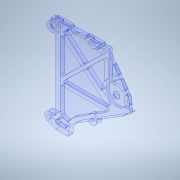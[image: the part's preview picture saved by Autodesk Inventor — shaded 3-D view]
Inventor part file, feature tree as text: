
AUTODESK INVENTOR PART (.ipt)
format: ipt  version: 2020.2 (Build 242310000, 310)  size: 1,882,112 bytes
history: native  units: mm
features: sketch x33, extrude x32, projected_geometry x28, fillet x11, other x4, hole x3
ambient origin geometry x8: Origin, YZ Plane, XZ Plane, XY Plane, X Axis, Y Axis, Z Axis, Center Point
bodies: Body1 (feature_tree)
feature tree (111):
  other  "ソリッド1"
  sketch  "スケッチ1"
  extrude  "押し出し1"  Depth=5.0mm
  extrude  "押し出し2"  Depth=3.0mm
  extrude  "押し出し3"  Depth=5.0mm
  extrude  "押し出し4"  Depth=3.0mm
  sketch  "スケッチ4"
  extrude  "押し出し5"  Depth=3.0mm
  extrude  "押し出し6"  Depth=5.0mm
  extrude  "押し出し7"  Depth=1.0mm
  sketch  "スケッチ6"
  extrude  "押し出し8"  Depth=5.0mm
  extrude  "押し出し9"  Depth=5.0mm
  sketch  "スケッチ8"
  extrude  "押し出し10"  Depth=2.0mm
  extrude  "押し出し11"  Depth=2.0mm
  extrude  "押し出し12"  Depth=2.0mm
  extrude  "押し出し13"  Depth=2.0mm
  sketch  "スケッチ9"
  extrude  "押し出し14"  Depth=2.0mm
  extrude  "押し出し15"  Depth=2.0mm
  sketch  "スケッチ10"
  sketch  "スケッチ11"
  sketch  "スケッチ12"
  sketch  "スケッチ13"
  extrude  "押し出し16"  Depth=2.0mm
  hole  "穴1"  [1 undecoded]
  fillet  "フィレット1"  Radius=2.0mm
  fillet  "フィレット2"  Radius=2.0mm
  sketch  "スケッチ14"
  sketch  "スケッチ15"
  extrude  "押し出し17"  Depth=2.0mm
  extrude  "押し出し18"  Depth=2.0mm
  sketch  "スケッチ16"
  extrude  "押し出し19"  Depth=5.0mm TaperAngle=0.0deg
  extrude  "押し出し20"  Depth=2.55mm TaperAngle=0.0deg
  hole  "穴2"  [1 undecoded]
  extrude  "押し出し21"  Depth=3.0mm TaperAngle=0.0deg
  fillet  "フィレット3"  Radius=2.0mm
  sketch  "スケッチ18"
  sketch  "スケッチ19"
  extrude  "押し出し22"  Depth=3.0mm TaperAngle=0.0deg
  fillet  "フィレット4"  Radius=3.0mm
  sketch  "スケッチ20"
  extrude  "押し出し23"  Depth=2.55mm TaperAngle=0.0deg
  fillet  "フィレット5"  Radius=5.0mm
  extrude  "押し出し24"  Depth=2.0mm TaperAngle=0.0deg
  fillet  "フィレット6"  Radius=9.0mm
  extrude  "押し出し25"  Depth=3.0mm
  fillet  "フィレット7"  Radius=10.0mm
  extrude  "押し出し26"  Depth=2.0mm
  fillet  "フィレット8"  Radius=2.0mm
  sketch  "スケッチ25"
  sketch  "スケッチ26"
  extrude  "押し出し27"  Depth=2.0mm
  sketch  "スケッチ27"
  sketch  "スケッチ28"
  extrude  "押し出し28"  Depth=2.0mm
  hole  "穴3"  [1 undecoded]
  fillet  "フィレット9"  Radius=3.0mm
  extrude  "押し出し29"  Depth=3.0mm
  extrude  "押し出し30"  Depth=3.0mm
  fillet  "フィレット10"  Radius=15.0mm
  extrude  "押し出し31"  Depth=15.0mm
  fillet  "フィレット11"  Radius=3.0mm
  sketch  "スケッチ32"
  extrude  "押し出し32"  Depth=3.0mm
  sketch  "スケッチ2"
  projected_geometry  "投影ループ1"
  sketch  "スケッチ3"
  projected_geometry  "投影ループ2"
  projected_geometry  "投影ループ3"
  sketch  "スケッチ5"
  projected_geometry  "投影ループ4"
  projected_geometry  "投影ループ5"
  projected_geometry  "投影ループ6"
  sketch  "スケッチ7"
  projected_geometry  "投影ループ7"
  projected_geometry  "投影ループ8"
  projected_geometry  "投影ループ9"
  projected_geometry  "投影ループ10"
  projected_geometry  "投影ループ11"
  projected_geometry  "投影ループ12"
  projected_geometry  "投影ループ13"
  projected_geometry  "投影ループ14"
  projected_geometry  "投影ループ15"
  sketch  "スケッチ17"
  projected_geometry  "投影ループ16"
  projected_geometry  "投影ループ17"
  projected_geometry  "投影ループ18"
  projected_geometry  "投影ループ19"
  sketch  "スケッチ21"
  projected_geometry  "投影ループ20"
  sketch  "スケッチ22"
  projected_geometry  "投影ループ21"
  sketch  "スケッチ23"
  projected_geometry  "投影ループ22"
  sketch  "スケッチ24"
  projected_geometry  "投影ループ23"
  projected_geometry  "投影ループ24"
  projected_geometry  "投影ループ25"
  projected_geometry  "投影ループ26"
  projected_geometry  "投影ループ27"
  sketch  "スケッチ29"
  sketch  "スケッチ30"
  sketch  "スケッチ31"
  projected_geometry  "投影ループ28"
  sketch  "スケッチ33"
  other  "断面エッジを投影1"
  other  "断面エッジを投影2"
  other  "断面エッジを投影3"
note: 3 required parameter values undecoded (feature->parameter linkage not recoverable at this tier; creation-order binding heuristic only, values carry confidence <= 0.55)
